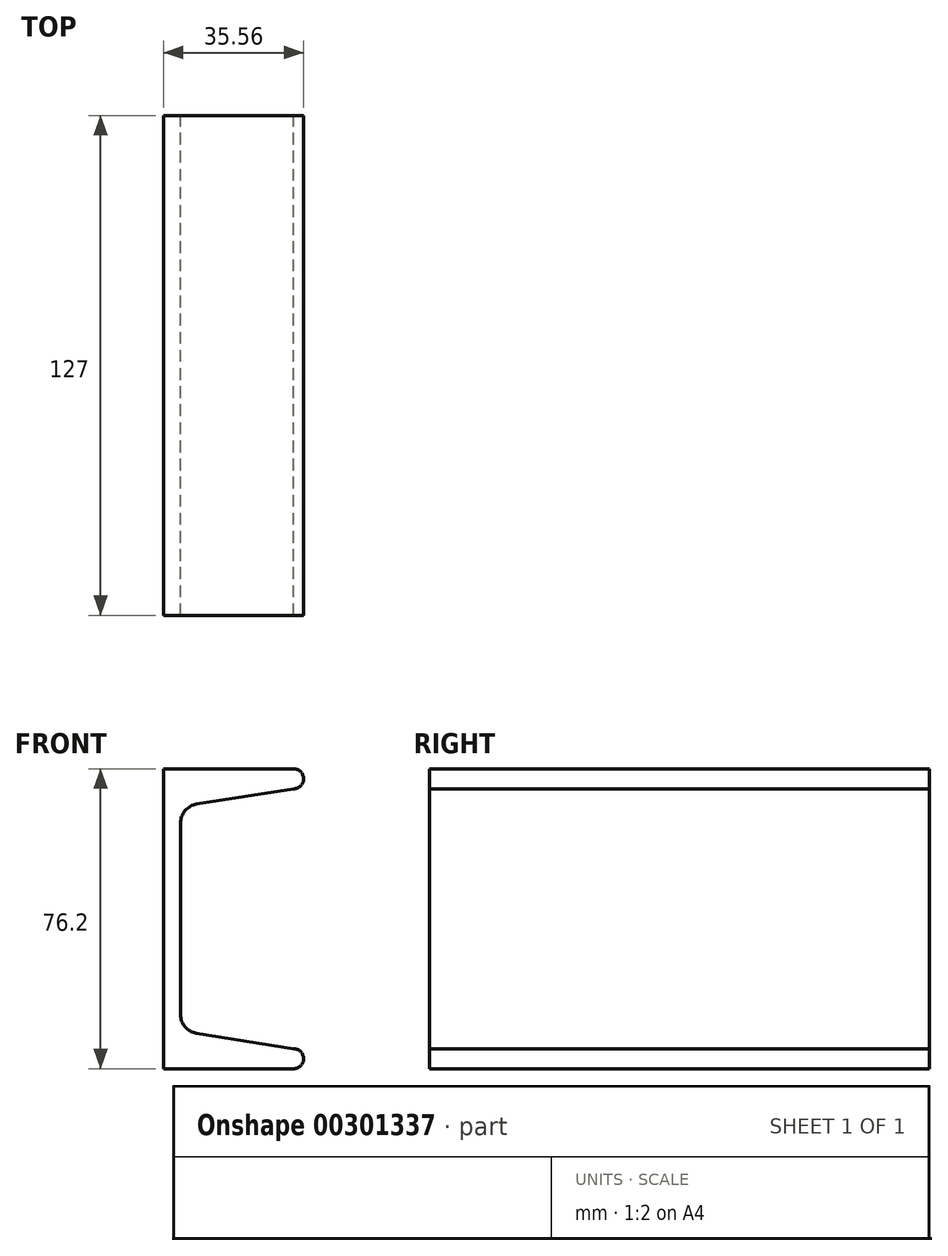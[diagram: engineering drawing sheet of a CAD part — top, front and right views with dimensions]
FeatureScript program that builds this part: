
annotation { "Feature Type Name" : "Feature", "Feature Type Description" : "" }
export const myFeature = defineFeature(function(context is Context, id is Id, definition is map)
    precondition{}
    {
        {
            var Q0;
            Q0=qCreatedBy(makeId("Front.planeOp"),FACE);
            var sketch = newSketch(context, id + "F0", { "sketchPlane" : qUnion([Q0])});
            skLineSegment(sketch, "E0", {"start": v(0, 0) * mm, "end": v(0, 38.1) * mm});
            skLineSegment(sketch, "E1", {"start": v(0, 38.1) * mm, "end": v(33.02, 38.1) * mm});
            skArc(sketch, "E2", {"start": v(33.02, 33.02) * mm, "mid": v(35.56, 35.56) * mm, "end": v(33.02, 38.1) * mm});
            skLineSegment(sketch, "E3", {"start": v(33.02, 33.02) * mm, "end": v(8.41, 29.12) * mm});
            skLineSegment(sketch, "E4", {"start": v(4.32, 24.33) * mm, "end": v(4.32, 0) * mm});
            skPoint(sketch, "E5.visualSharp", {"position": v(4.32, 28.47) * mm});
            skArc(sketch, "E5.filletArc", {"start": v(8.41, 29.12) * mm, "mid": v(5.48, 27.48) * mm, "end": v(4.32, 24.33) * mm});
            skArc(sketch, "E6.MirrorCS", {"start": v(33.02, -33.02) * mm, "mid": v(35.56, -35.56) * mm, "end": v(33.02, -38.1) * mm});
            skArc(sketch, "E7.MirrorCS", {"start": v(8.41, -29.12) * mm, "mid": v(5.48, -27.48) * mm, "end": v(4.32, -24.33) * mm});
            skLineSegment(sketch, "E8.MirrorCS", {"start": v(0, 0) * mm, "end": v(0, -38.1) * mm});
            skPoint(sketch, "E9.MirrorP", {"position": v(4.32, -28.47) * mm});
            skLineSegment(sketch, "E10.MirrorCS", {"start": v(33.02, -33.02) * mm, "end": v(8.41, -29.12) * mm});
            skLineSegment(sketch, "E11.MirrorCS", {"start": v(4.32, -24.33) * mm, "end": v(4.32, 0) * mm});
            skLineSegment(sketch, "E12.MirrorCS", {"start": v(0, -38.1) * mm, "end": v(33.02, -38.1) * mm});
            skSolve(sketch);
        }
        {
            var Q0;
            Q0=makeQuery(id+"F0.imprint","IMPRINT",FACE,{"disambiguationData":[TD([[makeQuery(id+"F0.imprint","IMPRINT",EDGE,{"derivedFrom":sQuery(id+"F0.wireOp",EDGE,"E0")}),-1.0]])]});
            extrude(context, id + "F1", {"entities" : qUnion([Q0]), "endBound" : BoundingType.SYMMETRIC, "depth" : 127 * mm});
        }
    });
